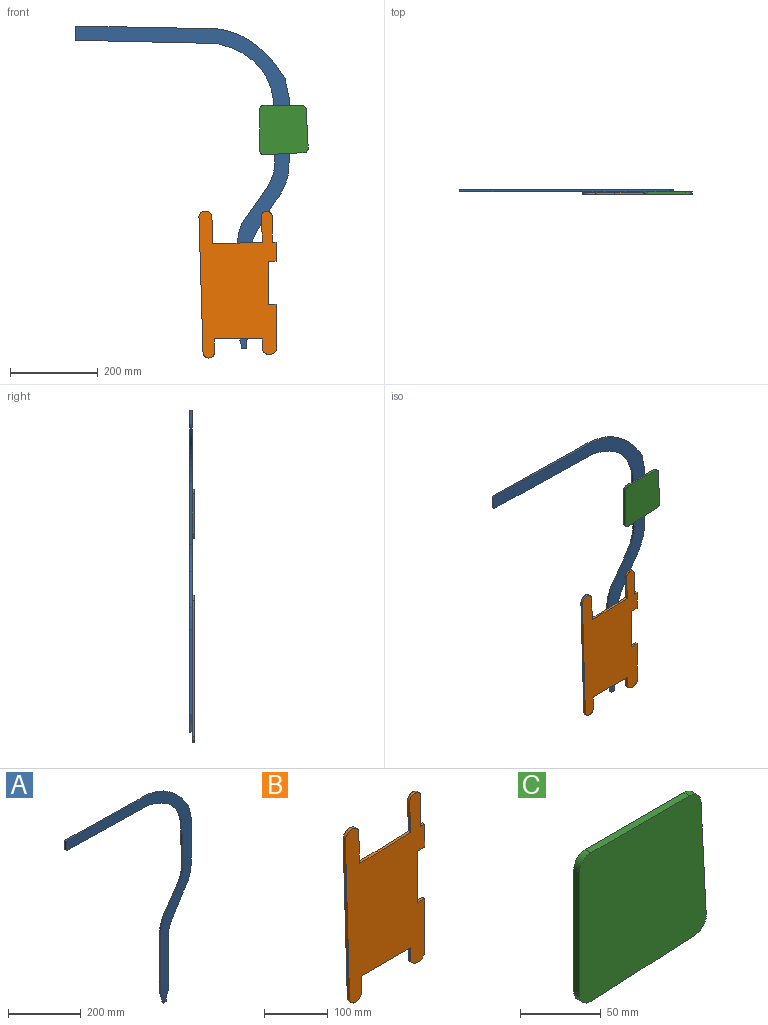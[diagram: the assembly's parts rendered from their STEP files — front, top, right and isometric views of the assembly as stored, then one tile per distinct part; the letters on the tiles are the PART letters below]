
ASSEMBLY  parts=3 mates=2
PART A: 22 faces, bbox 488.6x5x739.6 mm
  f0: extruded ~128.17x123.27mm, area 949.8mm2, adj f1,f19,f20,f21
  f1: plane 143.92x5mm, normal (-1,0,-0.03), area 719.9mm2, adj f0,f2,f20,f21
  f2: extruded ~60.47x17.66mm, area 320.1mm2, adj f1,f3,f20,f21
  f3: cylinder r=2559.16mm len=83.42mm, axis (0,-1,0), area 507.9mm2, adj f2,f4,f20,f21
  f4: extruded ~49.17x11.18mm, area 252.8mm2, adj f3,f5,f20,f21
  f5: plane 194.97x5mm, normal (-1,0,0), area 974.8mm2, adj f4,f6,f20,f21
  f6: extruded ~39.62x11.18mm, area 206.8mm2, adj f5,f7,f20,f21
  f7: plane 11.72x5mm, normal (0,0,-1), area 58.6mm2, adj f6,f8,f20,f21
  f8: plane 18.79x5mm, normal (1,0,0), area 94mm2, adj f7,f9,f20,f21
  f9: plane 20.83x10.25mm, normal (0.9,0,-0.44), area 116.1mm2, adj f8,f10,f20,f21
  f10: plane 179.59x5mm, normal (1,0,0.02), area 898.1mm2, adj f9,f11,f20,f21
  f11: extruded ~67.68x29.44mm, area 373.3mm2, adj f10,f12,f20,f21
  f12: plane 45.13x26.76mm, normal (0.86,0,-0.51), area 262.3mm2, adj f11,f13,f20,f21
  f13: extruded ~95.62x33.81mm, area 520mm2, adj f12,f14,f20,f21
  f14: plane 143.92x5mm, normal (1,0,0), area 719.6mm2, adj f13,f15,f20,f21
  f15: plane 42.73x9.07mm, normal (0.98,0,0.21), area 218.4mm2, adj f14,f16,f20,f21
  f16: extruded ~201.81x115.7mm, area 1232.5mm2, adj f15,f17,f20,f21
  f17: plane 275.12x5.43mm, normal (0.02,0,1), area 1375.9mm2, adj f16,f18,f20,f21
  f18: plane 32.58x5mm, normal (-1,0,0), area 162.9mm2, adj f17,f19,f20,f21
  f19: plane 321.27x7.24mm, normal (-0.02,0,-1), area 1606.8mm2, adj f0,f18,f20,f21
  f20: plane 739.61x488.62mm, normal (0,-1,0), area 37269.4mm2, adj f0,f1,f2,f3,f4,f5,f6,f7
  f21: plane 739.61x488.62mm, normal (0,1,0), area 37269.4mm2, adj f0,f1,f2,f3,f4,f5,f6,f7
PART B: 21 faces, bbox 175.8x5x335.1 mm
  f0: plane 109.42x5mm, normal (0,0,-1), area 547.1mm2, adj f1,f18,f19,f20
  f1: plane 26.9x5mm, normal (-1,0,0), area 134.5mm2, adj f0,f2,f19,f20
  f2: cylinder r=18.11mm len=30.99mm, axis (0,1,0), area 185.9mm2, adj f1,f3,f19,f20
  f3: plane 105.52x5mm, normal (1,0,0), area 527.6mm2, adj f2,f4,f19,f20
  f4: plane 17.45x5mm, normal (0,0,1), area 87.2mm2, adj f3,f5,f19,f20
  f5: plane 98.21x5mm, normal (1,0,0), area 491.1mm2, adj f4,f6,f19,f20
  f6: plane 17.45x5mm, normal (0,0,-1), area 87.2mm2, adj f5,f7,f19,f20
  f7: plane 43.72x5mm, normal (1,0,0), area 218.6mm2, adj f6,f8,f19,f20
  f8: plane 9.11x5mm, normal (0,0,1), area 45.5mm2, adj f7,f9,f19,f20
  f9: plane 55.95x5mm, normal (1,0,0), area 279.8mm2, adj f8,f10,f19,f20
  f10: cylinder r=12.52mm len=25.04mm, axis (0,1,0), area 215.5mm2, adj f9,f11,f19,f20
  f11: plane 55.95x5mm, normal (-1,0,-0.05), area 280.1mm2, adj f10,f12,f19,f20
  f12: plane 72.01x5mm, normal (-0.04,0,1), area 360.3mm2, adj f11,f13,f19,f20
  f13: plane 41.21x5mm, normal (0,0,1), area 206mm2, adj f12,f14,f19,f20
  f14: plane 62.25x5mm, normal (1,0,0.03), area 311.4mm2, adj f13,f15,f19,f20
  f15: cylinder r=15.08mm len=29.48mm, axis (0,1,0), area 205.2mm2, adj f14,f16,f19,f20
  f16: plane 310.09x9.29mm, normal (-1,0,-0.03), area 1551.2mm2, adj f15,f17,f19,f20
  f17: cylinder r=13.08mm len=26.14mm, axis (0,1,0), area 203.7mm2, adj f16,f18,f19,f20
  f18: plane 30.17x5mm, normal (1,0,0), area 150.9mm2, adj f0,f17,f19,f20
  f19: plane 335.06x175.84mm, normal (0,-1,0), area 41464mm2, adj f0,f1,f2,f3,f4,f5,f6,f7
  f20: plane 335.06x175.84mm, normal (0,1,0), area 41464mm2, adj f0,f1,f2,f3,f4,f5,f6,f7
PART C: 10 faces, bbox 110.8x5x112.6 mm
  f0: plane 90.8x5mm, normal (0.05,0,-1), area 454.6mm2, adj f1,f7,f8,f9
  f1: cylinder r=10mm len=10.51mm, axis (0,1,0), area 78.5mm2, adj f0,f2,f8,f9
  f2: plane 87.84x5mm, normal (1,0,0.05), area 439.8mm2, adj f1,f3,f8,f9
  f3: cylinder r=10mm len=9.99mm, axis (0,1,0), area 75.9mm2, adj f2,f4,f8,f9
  f4: plane 86.21x5mm, normal (0,0,1), area 431mm2, adj f3,f5,f8,f9
  f5: cylinder r=10mm len=10mm, axis (0,1,0), area 78.5mm2, adj f4,f6,f8,f9
  f6: plane 92.58x5mm, normal (-1,0,0), area 462.9mm2, adj f5,f7,f8,f9
  f7: cylinder r=10mm len=10.52mm, axis (0,1,0), area 81.1mm2, adj f0,f6,f8,f9
  f8: plane 112.58x110.8mm, normal (0,-1,0), area 11879.8mm2, adj f0,f1,f2,f3,f4,f5,f6,f7
  f9: plane 112.58x110.8mm, normal (0,1,0), area 11879.8mm2, adj f0,f1,f2,f3,f4,f5,f6,f7
PLACE A t=(-498.18,-272.21,-351.48)mm
PLACE B t=(-511.49,-277.21,-333.71)mm
PLACE C t=(-491.87,-277.21,-316.59)mm
MATE planar A.f20 <-> C.f9  axis (0,-1,0) through (11.5,-277.21,228.39)mm
MATE planar A.f20 <-> B.f20  axis (0,-1,0) through (-107.68,-277.21,-134.11)mm
